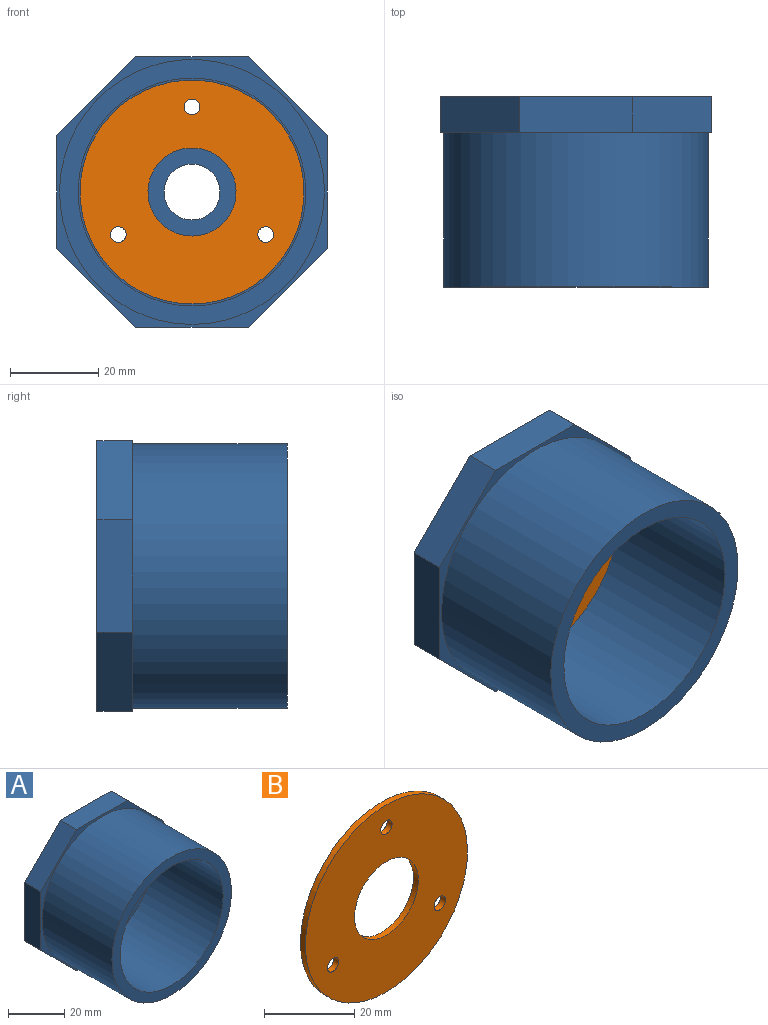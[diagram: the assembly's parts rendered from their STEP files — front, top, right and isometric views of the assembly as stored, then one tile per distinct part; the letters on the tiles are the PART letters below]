
ASSEMBLY  parts=2 mates=1
PART A: 20 faces, bbox 61.5x43.2x61.5 mm
  f0: plane 25.46x8.13mm, normal (0,0,1), area 206.9mm2, adj f1,f7,f8,f9
  f1: plane 18x18mm, normal (-0.71,0,0.71), area 206.9mm2, adj f0,f2,f8,f9
  f2: plane 25.46x8.13mm, normal (-1,0,0), area 206.9mm2, adj f1,f3,f8,f9
  f3: plane 18x18mm, normal (-0.71,0,-0.71), area 206.9mm2, adj f2,f4,f8,f9
  f4: plane 25.46x8.13mm, normal (0,0,-1), area 206.9mm2, adj f3,f5,f8,f9
  f5: plane 18x18mm, normal (0.71,0,-0.71), area 206.9mm2, adj f4,f6,f8,f9
  f6: plane 25.46x8.13mm, normal (1,0,0), area 206.9mm2, adj f5,f7,f8,f9
  f7: plane 18x18mm, normal (0.71,0,0.71), area 206.9mm2, adj f0,f6,f8,f9
  f8: plane 61.47x61.47mm, normal (0,-1,0), area 295.9mm2, adj f0,f1,f2,f3,f4,f5,f6,f7
  f9: plane 61.47x61.47mm, normal (0,1,0), area 2973.6mm2, adj f0,f1,f2,f3,f4,f5,f6,f7
  f10: cylinder r=25.84mm len=51.69mm, axis (0,1,0), area 5691.9mm2, adj f12,f13
  f11: cylinder r=30.04mm len=60.07mm, axis (0,1,0), area 6615mm2, adj f8,f12
  f12: plane 60.07x60.07mm, normal (0,-1,0), area 735.7mm2, adj f10,f11
  f13: plane 51.69x51.69mm, normal (0,-1,0), area 1754.8mm2, adj f10,f14,f17,f18,f19
  f14: cylinder r=9.99mm len=19.99mm, axis (0,-1,0), area 350.9mm2, adj f13,f15
  f15: plane 19.99x19.99mm, normal (0,-1,0), area 187.2mm2, adj f14,f16
  f16: cylinder r=6.35mm len=12.7mm, axis (0,-1,0), area 101.3mm2, adj f9,f15
  f17: cylinder r=1.78mm len=8.13mm, axis (0,-1,0), area 90.8mm2, adj f9,f13
  f18: cylinder r=1.78mm len=8.13mm, axis (0,-1,0), area 90.8mm2, adj f9,f13
  f19: cylinder r=1.78mm len=8.13mm, axis (0,-1,0), area 90.8mm2, adj f9,f13
PART B: 7 faces, bbox 50.8x1.5x50.8 mm
  f0: cylinder r=9.99mm len=19.99mm, axis (0,1,0), area 95.7mm2, adj f2,f3
  f1: cylinder r=25.4mm len=50.8mm, axis (0,1,0), area 243.2mm2, adj f2,f3
  f2: plane 50.8x50.8mm, normal (0,-1,0), area 1683.2mm2, adj f0,f1,f4,f5,f6
  f3: plane 50.8x50.8mm, normal (0,1,0), area 1683.2mm2, adj f0,f1,f4,f5,f6
  f4: cylinder r=1.78mm len=3.56mm, axis (0,-1,0), area 17mm2, adj f2,f3
  f5: cylinder r=1.78mm len=3.56mm, axis (0,-1,0), area 17mm2, adj f2,f3
  f6: cylinder r=1.78mm len=3.56mm, axis (0,-1,0), area 17mm2, adj f2,f3
PLACE A at identity
PLACE B t=(0,-8.13,0)mm
MATE fastened B.f1 <-> A.f11  axis (0,1,0) through (0,-8.13,0)mm
